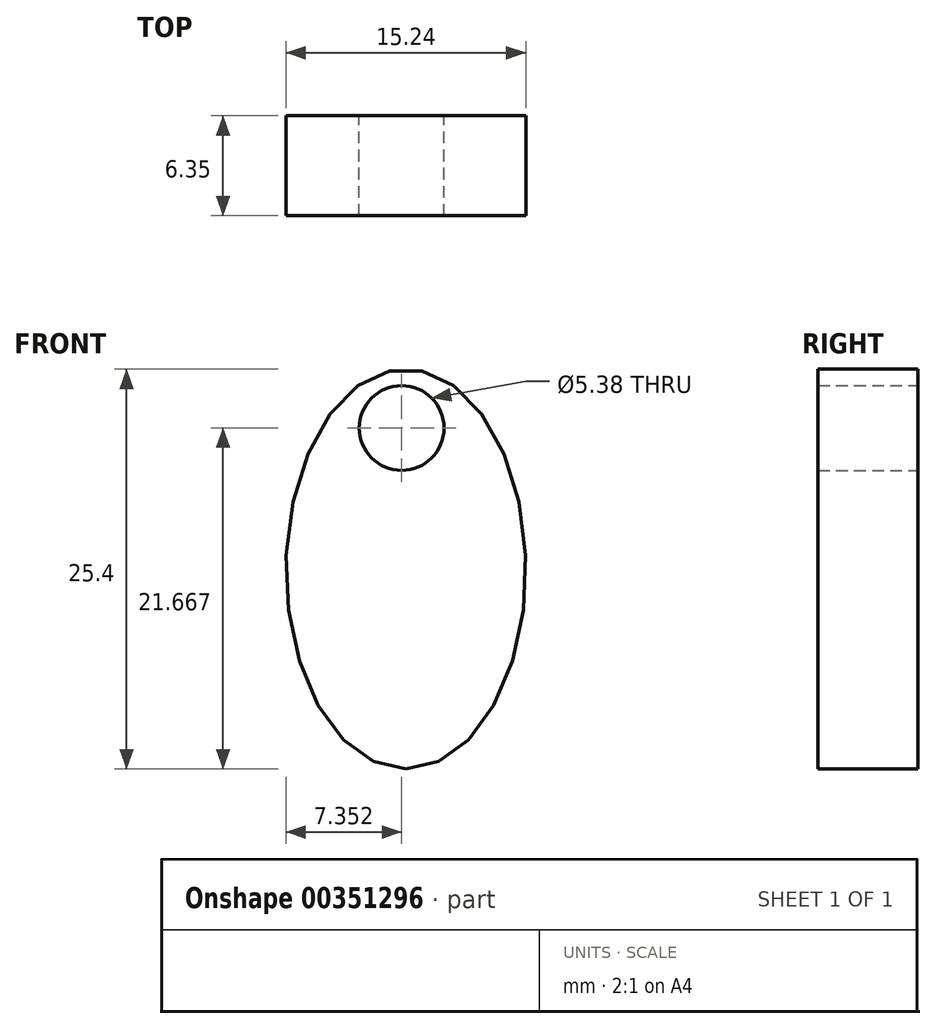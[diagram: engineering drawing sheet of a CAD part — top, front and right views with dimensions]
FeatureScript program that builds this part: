
annotation { "Feature Type Name" : "Feature", "Feature Type Description" : "" }
export const myFeature = defineFeature(function(context is Context, id is Id, definition is map)
    precondition{}
    {
        {
            var Q0;
            Q0=qCreatedBy(makeId("Front.planeOp"),FACE);
            var sketch = newSketch(context, id + "F0", { "sketchPlane" : qUnion([Q0])});
            skEllipse(sketch, "E0", {"center": v(-38.5, 26.38) * mm, "majorRadius": 12.7 * mm, "minorRadius": 7.62 * mm, "majorAxis": v(0, -1)});
            skCircle(sketch, "E1", {"center": v(-38.78, 35.35) * mm, "radius": 2.7 * mm});
            skSolve(sketch);
        }
        {
            var Q0;
            Q0=makeQuery(id+"F0.imprint","IMPRINT",FACE,{"disambiguationData":[TD([[makeQuery(id+"F0.imprint","IMPRINT",EDGE,{"derivedFrom":sQuery(id+"F0.wireOp",EDGE,"E0")}),1.0]])]});
            extrude(context, id + "F1", {"entities" : qUnion([Q0]), "depth" : 6.35 * mm});
        }
    });
